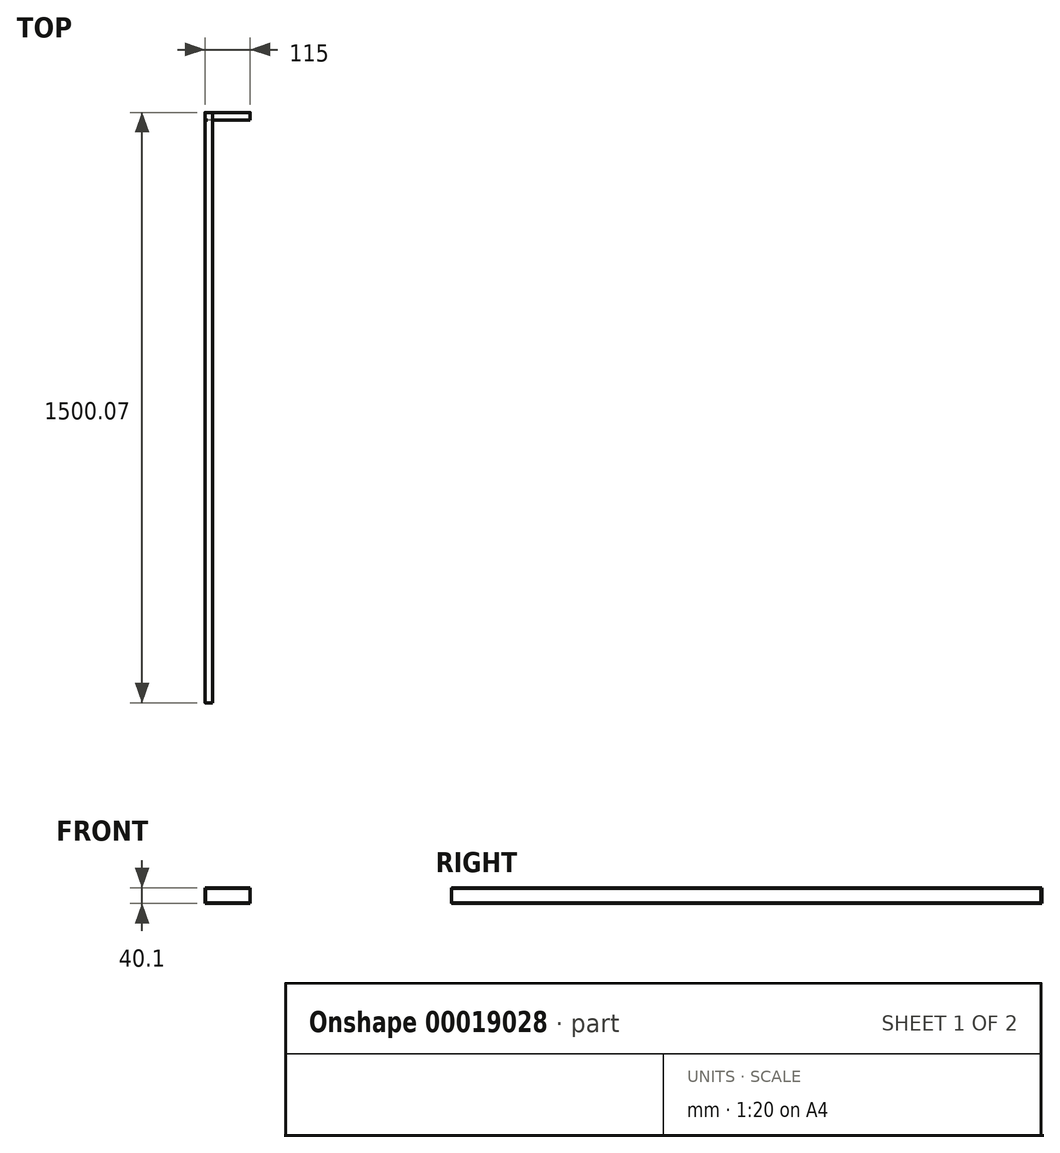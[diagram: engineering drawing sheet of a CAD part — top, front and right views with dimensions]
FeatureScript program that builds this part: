
annotation { "Feature Type Name" : "Feature", "Feature Type Description" : "" }
export const myFeature = defineFeature(function(context is Context, id is Id, definition is map)
    precondition{}
    {
        {
            var Q0;
            Q0=qCreatedBy(makeId("Front.planeOp"),FACE);
            var sketch = newSketch(context, id + "F0", { "sketchPlane" : qUnion([Q0])});
            skLineSegment(sketch, "E0", {"start": v(7, 0) * mm, "end": v(20, 0) * mm});
            skLineSegment(sketch, "E1", {"start": v(20, 0) * mm, "end": v(20, -2) * mm});
            skLineSegment(sketch, "E2", {"start": v(20, -2) * mm, "end": v(7, -2) * mm});
            skLineSegment(sketch, "E3", {"start": v(2, -7) * mm, "end": v(2, -33) * mm});
            skLineSegment(sketch, "E4", {"start": v(7, -38) * mm, "end": v(20, -38) * mm});
            skLineSegment(sketch, "E5", {"start": v(20, -38) * mm, "end": v(20, -40) * mm});
            skLineSegment(sketch, "E6", {"start": v(20, -40) * mm, "end": v(7, -40) * mm});
            skLineSegment(sketch, "E7", {"start": v(0, -33) * mm, "end": v(0, -7) * mm});
            skPoint(sketch, "E8.visualSharp", {"position": v(2, -2) * mm});
            skArc(sketch, "E8.filletArc", {"start": v(7, -2) * mm, "mid": v(3.46, -3.46) * mm, "end": v(2, -7) * mm});
            skPoint(sketch, "E9.visualSharp", {"position": v(2, -38) * mm});
            skArc(sketch, "E9.filletArc", {"start": v(2, -33) * mm, "mid": v(3.46, -36.54) * mm, "end": v(7, -38) * mm});
            skPoint(sketch, "E10.visualSharp", {"position": v(0, -40) * mm});
            skArc(sketch, "E10.filletArc", {"start": v(0, -33) * mm, "mid": v(2.05, -37.95) * mm, "end": v(7, -40) * mm});
            skPoint(sketch, "E11.visualSharp", {"position": v(0, 0) * mm});
            skArc(sketch, "E11.filletArc", {"start": v(7, 0) * mm, "mid": v(2.05, -2.05) * mm, "end": v(0, -7) * mm});
            skSolve(sketch);
        }
        {
            var Q0;
            Q0 = qSketchRegion(id + "F0", true);
            extrude(context, id + "F1", {"entities" : qUnion([Q0]), "depth" : 1500 * mm, "offsetDistance" : 25 * mm});
        }
        {
            var Q0;
            Q0=qCreatedBy(makeId("Right.planeOp"),FACE);
            var sketch = newSketch(context, id + "F2", { "sketchPlane" : qUnion([Q0])});
            skLineSegment(sketch, "E12", {"start": v(-6.93, -40.1) * mm, "end": v(-19.93, -40.1) * mm});
            skLineSegment(sketch, "E13", {"start": v(-19.93, -40.1) * mm, "end": v(-19.93, -38.1) * mm});
            skLineSegment(sketch, "E14", {"start": v(-19.93, -38.1) * mm, "end": v(-6.93, -38.1) * mm});
            skLineSegment(sketch, "E15", {"start": v(-1.93, -33.1) * mm, "end": v(-1.93, -7.1) * mm});
            skLineSegment(sketch, "E16", {"start": v(-6.93, -2.1) * mm, "end": v(-19.93, -2.1) * mm});
            skLineSegment(sketch, "E17", {"start": v(-19.93, -2.1) * mm, "end": v(-19.93, -0.1) * mm});
            skLineSegment(sketch, "E18", {"start": v(-19.93, -0.1) * mm, "end": v(-6.93, -0.1) * mm});
            skLineSegment(sketch, "E19", {"start": v(0.07, -7.1) * mm, "end": v(0.07, -33.1) * mm});
            skPoint(sketch, "E20.visualSharp", {"position": v(-1.93, -38.1) * mm});
            skArc(sketch, "E20.filletArc", {"start": v(-6.93, -38.1) * mm, "mid": v(-3.39, -36.63) * mm, "end": v(-1.93, -33.1) * mm});
            skPoint(sketch, "E21.visualSharp", {"position": v(-1.93, -2.1) * mm});
            skArc(sketch, "E21.filletArc", {"start": v(-1.93, -7.1) * mm, "mid": v(-3.39, -3.56) * mm, "end": v(-6.93, -2.1) * mm});
            skPoint(sketch, "E22.visualSharp", {"position": v(0.07, -0.1) * mm});
            skArc(sketch, "E22.filletArc", {"start": v(0.07, -7.1) * mm, "mid": v(-1.98, -2.15) * mm, "end": v(-6.93, -0.1) * mm});
            skPoint(sketch, "E23.visualSharp", {"position": v(0.07, -40.1) * mm});
            skArc(sketch, "E23.filletArc", {"start": v(-6.93, -40.1) * mm, "mid": v(-1.98, -38.05) * mm, "end": v(0.07, -33.1) * mm});
            skSolve(sketch);
        }
        {
            var Q0;
            Q0 = qSketchRegion(id + "F2", true);
            extrude(context, id + "F3", {"entities" : qUnion([Q0]), "depth" : 115 * mm, "offsetDistance" : 25 * mm});
        }
    });
